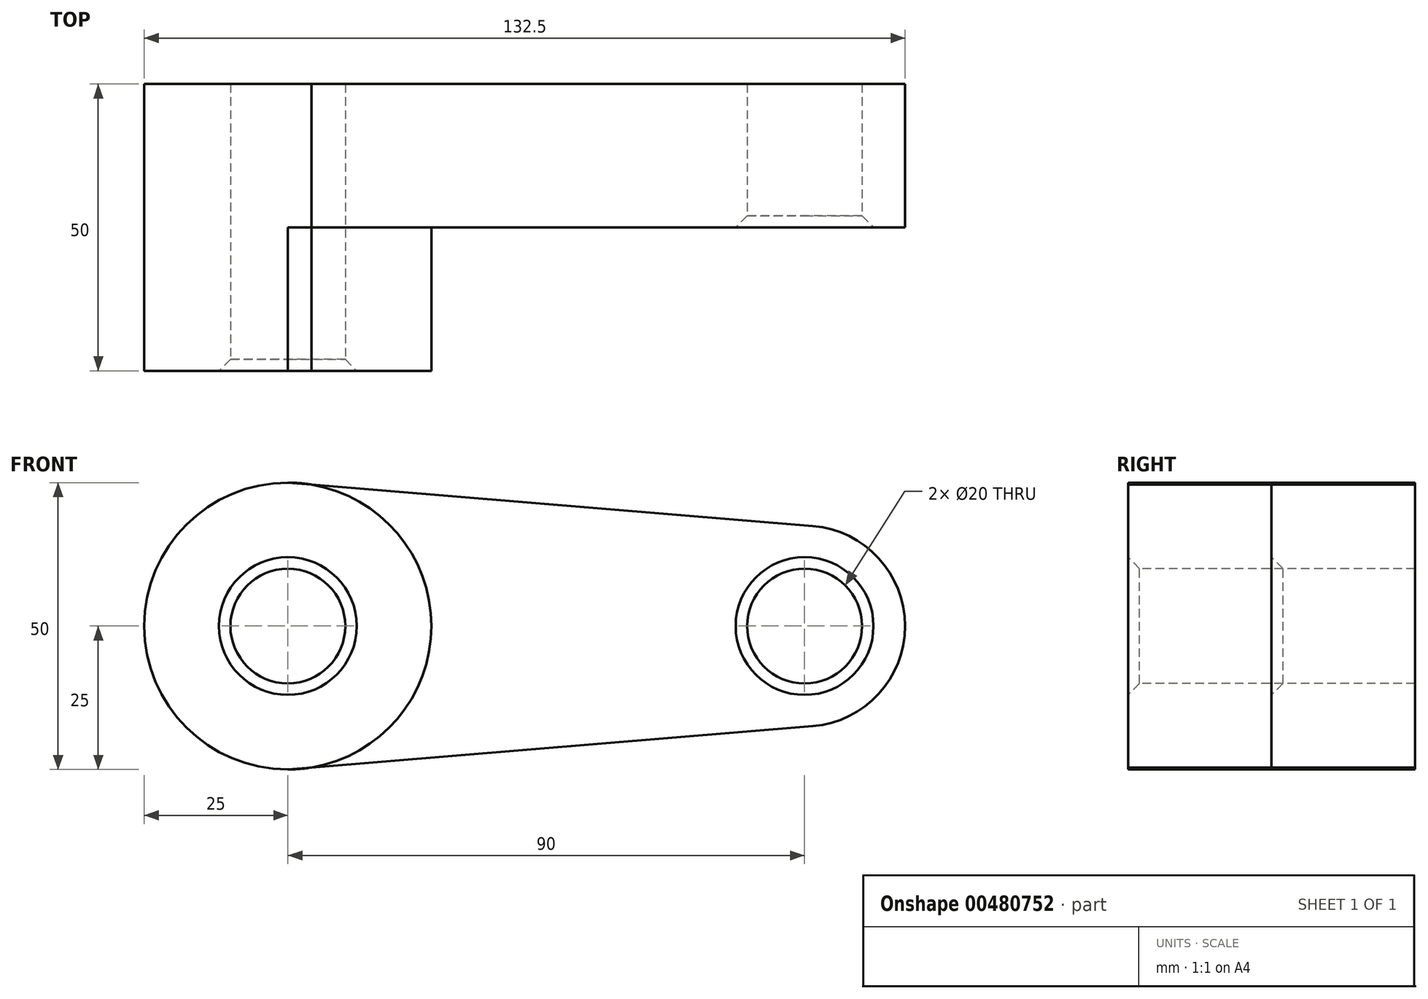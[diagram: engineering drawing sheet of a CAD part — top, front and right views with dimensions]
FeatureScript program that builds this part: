
annotation { "Feature Type Name" : "Feature", "Feature Type Description" : "" }
export const myFeature = defineFeature(function(context is Context, id is Id, definition is map)
    precondition{}
    {
        {
            var Q0;
            Q0=qCreatedBy(makeId("Front.planeOp"),FACE);
            var sketch = newSketch(context, id + "F0", { "sketchPlane" : qUnion([Q0])});
            skCircle(sketch, "E0", {"center": v(0, 0) * mm, "radius": 25 * mm});
            skCircle(sketch, "E1", {"center": v(90, 0) * mm, "radius": 17.5 * mm});
            skLineSegment(sketch, "E2", {"start": v(0, 25) * mm, "end": v(91.44, 17.44) * mm});
            skLineSegment(sketch, "E3", {"start": v(0, -25) * mm, "end": v(91.44, -17.44) * mm});
            skCircle(sketch, "E4", {"center": v(0, 0) * mm, "radius": 10 * mm});
            skCircle(sketch, "E5", {"center": v(90, 0) * mm, "radius": 10 * mm});
            skSolve(sketch);
        }
        {
            var Q0;
            Q0 = qSketchRegion(id + "F0", true);
            extrude(context, id + "F1", {"entities" : qUnion([Q0]), "oppositeDirection" : true, "depth" : 25 * mm});
        }
        {
            var Q0;
            Q0=makeQuery(id+"F0.imprint","IMPRINT",FACE,{"disambiguationData":[TD([[makeQuery(id+"F0.imprint","IMPRINT",EDGE,{"derivedFrom":sQuery(id+"F0.wireOp",EDGE,"E4")}),-1.0]])]});
            extrude(context, id + "F2", {"entities" : qUnion([Q0]), "operationType" : NewBodyOperationType.ADD, "depth" : 25 * mm});
        }
        {
            var Q0;
            {var subQ0=sQuery(id+"F0.wireOp",EDGE,"E0");Q0=makeQuery(id+"F2.opExtrude","CAP_EDGE",EDGE,{"disambiguationData":[OSD([subQ0]),TDD([makeQuery(id+"F0.imprint","IMPRINT",EDGE,{"disambiguationData":[TD([[makeQuery(id+"F0.imprint","INTERSECT",VERTEX,{"disambiguationData":[OD(1.0)],"derivedFrom":[subQ0,sQuery(id+"F0.wireOp",EDGE,"E2")]}),1.0]])],"derivedFrom":subQ0})])],"isStart":false});}
            var Q1;
            Q1=makeQuery(id+"F1.opExtrude","CAP_EDGE",EDGE,{"disambiguationData":[OSD([sQuery(id+"F0.wireOp",EDGE,"E5")])],"isStart":true});
            var Q2;
            Q2=makeQuery(id+"F2.opExtrude","CAP_EDGE",EDGE,{"disambiguationData":[OSD([sQuery(id+"F0.wireOp",EDGE,"E4")])],"isStart":false});
            chamfer(context, id + "F3", {"entities" : qUnion([Q0, Q1, Q2]), "width" : 2 * mm, "tangentPropagation" : true});
        }
    });
